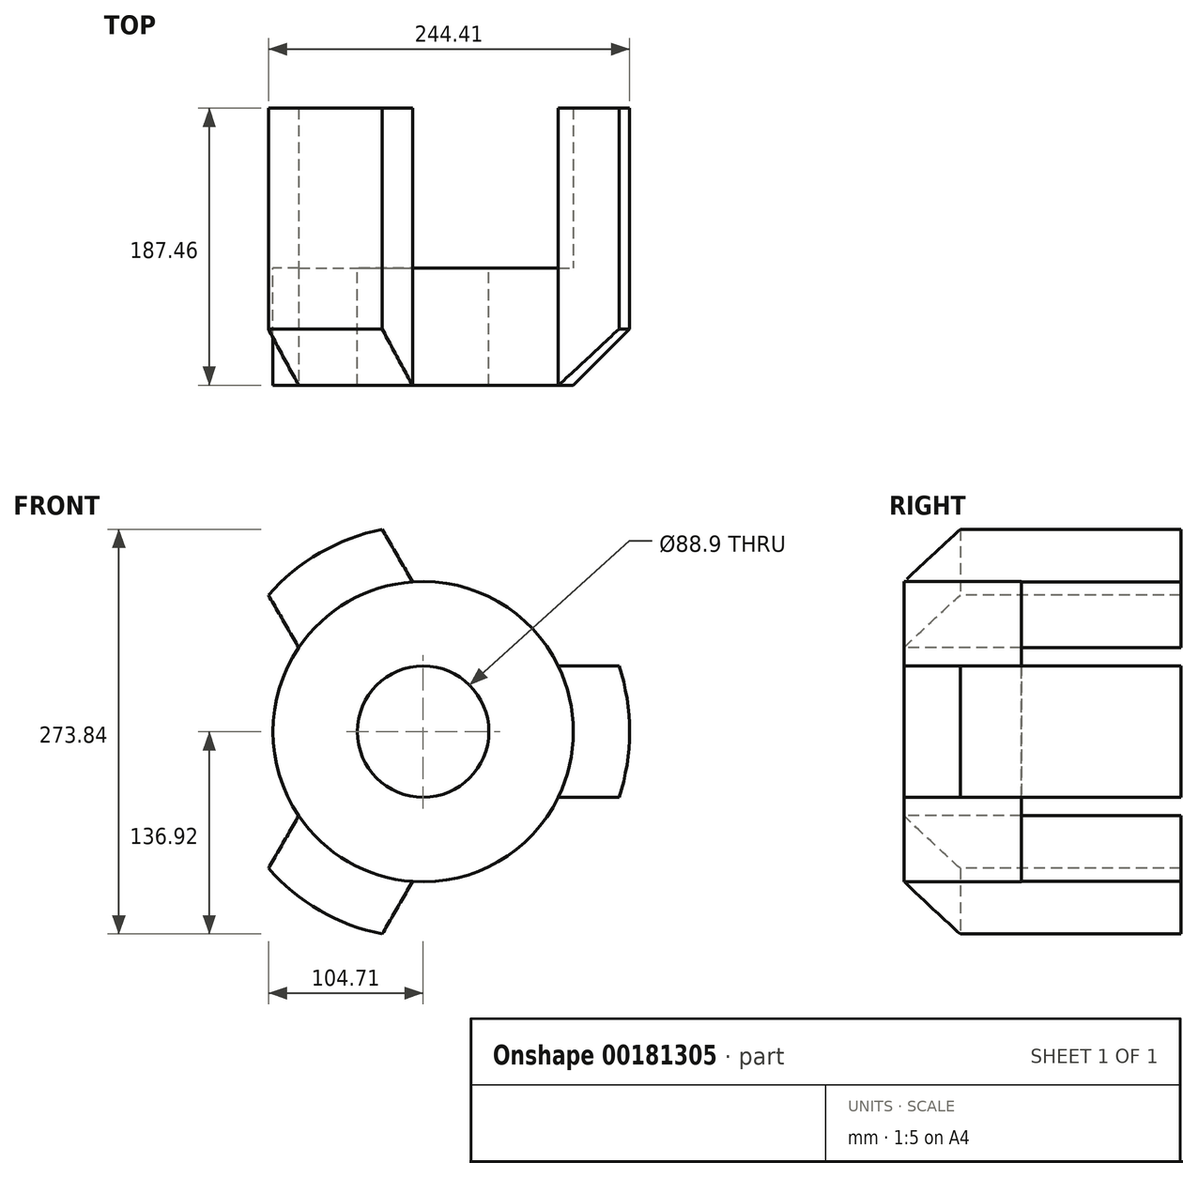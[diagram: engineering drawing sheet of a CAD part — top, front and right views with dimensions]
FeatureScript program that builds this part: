
annotation { "Feature Type Name" : "Feature", "Feature Type Description" : "" }
export const myFeature = defineFeature(function(context is Context, id is Id, definition is map)
    precondition{}
    {
        {
            var Q0;
            Q0=qCreatedBy(makeId("Front.planeOp"),FACE);
            var sketch = newSketch(context, id + "F0", { "sketchPlane" : qUnion([Q0])});
            skCircle(sketch, "E0", {"center": v(0, 0) * mm, "radius": 101.6 * mm});
            skCircle(sketch, "E1", {"center": v(0, 0) * mm, "radius": 44.45 * mm});
            skSolve(sketch);
        }
        {
            var Q0;
            Q0 = qSketchRegion(id + "F0", true);
            extrude(context, id + "F1", {"entities" : qUnion([Q0]), "depth" : 79.38 * mm});
        }
        {
            var Q0;
            Q0=makeQuery(id+"F1.opExtrude","CAP_FACE",FACE,{"disambiguationData":[OSD([sQuery(id+"F0.wireOp",EDGE,"E0"),sQuery(id+"F0.wireOp",EDGE,"E1")])],"isStart":false});
            var sketch = newSketch(context, id + "F2", { "sketchPlane" : qUnion([Q0])});
            skLineSegment(sketch, "E2", {"start": v(91.36, 44.45) * mm, "end": v(132.44, 44.45) * mm});
            skLineSegment(sketch, "E3", {"start": v(132.44, -44.45) * mm, "end": v(91.36, -44.45) * mm});
            skPoint(sketch, "E4.end.orphan", {"position": v(101.6, 0) * mm});
            skPoint(sketch, "E4.start.orphan", {"position": v(139.7, 0) * mm});
            skArc(sketch, "E5", {"start": v(91.36, -44.45) * mm, "mid": v(101.6, 0) * mm, "end": v(91.36, 44.45) * mm});
            skArc(sketch, "E6", {"start": v(132.44, -44.45) * mm, "mid": v(139.7, 0) * mm, "end": v(132.44, 44.45) * mm});
            skPoint(sketch, "E7.orphan", {"position": v(139.7, -44.45) * mm});
            skLineSegment(sketch, "E8.1.0", {"start": v(-84.18, 56.9) * mm, "end": v(-104.71, 92.47) * mm});
            skArc(sketch, "E8.1.1", {"start": v(-27.73, 136.92) * mm, "mid": v(-69.85, 120.98) * mm, "end": v(-104.71, 92.47) * mm});
            skLineSegment(sketch, "E8.1.2", {"start": v(-27.73, 136.92) * mm, "end": v(-7.19, 101.35) * mm});
            skArc(sketch, "E8.1.3", {"start": v(-7.19, 101.35) * mm, "mid": v(-50.8, 87.99) * mm, "end": v(-84.18, 56.9) * mm});
            skLineSegment(sketch, "E8.2.0", {"start": v(-7.19, -101.35) * mm, "end": v(-27.73, -136.92) * mm});
            skArc(sketch, "E8.2.1", {"start": v(-104.71, -92.47) * mm, "mid": v(-69.85, -120.98) * mm, "end": v(-27.73, -136.92) * mm});
            skLineSegment(sketch, "E8.2.2", {"start": v(-104.71, -92.47) * mm, "end": v(-84.18, -56.9) * mm});
            skArc(sketch, "E8.2.3", {"start": v(-84.18, -56.9) * mm, "mid": v(-50.8, -87.99) * mm, "end": v(-7.19, -101.35) * mm});
            skSolve(sketch);
        }
        {
            var Q0;
            Q0 = qSketchRegion(id + "F2", true);
            extrude(context, id + "F3", {"entities" : qUnion([Q0]), "operationType" : NewBodyOperationType.ADD, "oppositeDirection" : true, "depth" : 187.45 * mm});
        }
        {
            var Q0;
            Q0=makeQuery(id+"F3.opExtrude","CAP_EDGE",EDGE,{"disambiguationData":[OSD([sQuery(id+"F2.wireOp",EDGE,"E6")])],"isStart":true});
            chamfer(context, id + "F4", {"entities" : qUnion([Q0]), "width" : 38.1 * mm, "tangentPropagation" : true});
        }
        {
            var Q0;
            Q0=makeQuery(id+"F3.opExtrude","CAP_EDGE",EDGE,{"disambiguationData":[OSD([sQuery(id+"F2.wireOp",EDGE,"E8.2.1")])],"isStart":true});
            chamfer(context, id + "F5", {"entities" : qUnion([Q0]), "width" : 38.1 * mm, "tangentPropagation" : true});
        }
        {
            var Q0;
            Q0=makeQuery(id+"F3.opExtrude","CAP_EDGE",EDGE,{"disambiguationData":[OSD([sQuery(id+"F2.wireOp",EDGE,"E8.1.1")])],"isStart":true});
            chamfer(context, id + "F6", {"entities" : qUnion([Q0]), "width" : 38.1 * mm, "tangentPropagation" : true});
        }
    });
